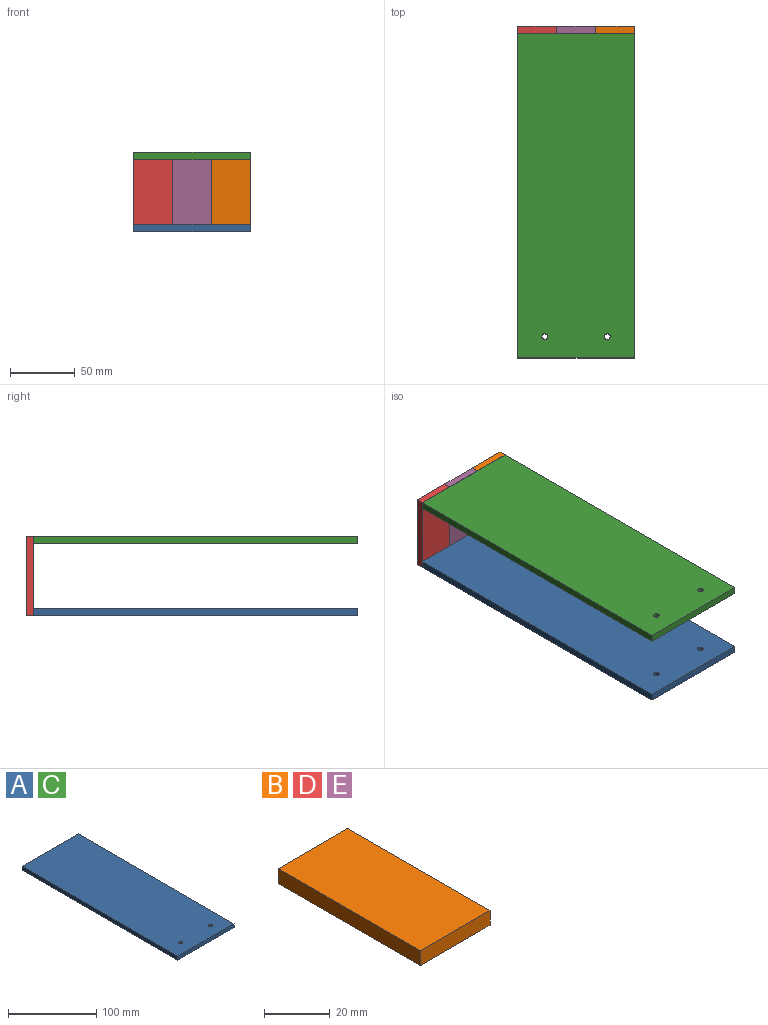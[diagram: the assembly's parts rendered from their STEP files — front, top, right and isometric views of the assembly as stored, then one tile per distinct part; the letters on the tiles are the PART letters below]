
ASSEMBLY  parts=5 mates=4
PART A: 10 faces, bbox 90x250x5.5 mm
  f0: plane 90x5.5mm, normal (0,1,0), area 495mm2, adj f1,f5,f6,f7
  f1: plane 250x5.5mm, normal (-1,0,0), area 1375mm2, adj f0,f2,f6,f7
  f2: plane 90x5.5mm, normal (0,-1,0), area 495mm2, adj f1,f5,f6,f7
  f3: cylinder r=2.25mm len=4.5mm, axis (0,0,-1), area 35.3mm2, adj f6,f8
  f4: cylinder r=2.25mm len=4.5mm, axis (0,0,-1), area 35.3mm2, adj f6,f9
  f5: plane 250x5.5mm, normal (1,0,0), area 1375mm2, adj f0,f2,f6,f7
  f6: plane 250x90mm, normal (0,0,1), area 22468.2mm2, adj f0,f1,f2,f3,f4,f5
  f7: plane 250x90mm, normal (0,0,-1), area 22326.8mm2, adj f0,f1,f2,f5,f8,f9
  f8: cone r=5.25mm half-angle=45deg, axis (0,0,-1), area 100mm2, adj f3,f7
  f9: cone r=5.25mm half-angle=45deg, axis (0,0,-1), area 100mm2, adj f4,f7
PART B: 6 faces, bbox 30x61x5.5 mm
  f0: plane 30x5.5mm, normal (0,1,0), area 165mm2, adj f1,f3,f4,f5
  f1: plane 61x5.5mm, normal (-1,0,0), area 335.5mm2, adj f0,f2,f4,f5
  f2: plane 30x5.5mm, normal (0,-1,0), area 165mm2, adj f1,f3,f4,f5
  f3: plane 61x5.5mm, normal (1,0,0), area 335.5mm2, adj f0,f2,f4,f5
  f4: plane 61x30mm, normal (0,0,1), area 1830mm2, adj f0,f1,f2,f3
  f5: plane 61x30mm, normal (0,0,-1), area 1830mm2, adj f0,f1,f2,f3
PART C: same geometry as A
PART D: same geometry as B
PART E: same geometry as B
PLACE A t=(-40.4,-87.75,38.5)mm
PLACE B rot(axis=(1,0,0),90deg) t=(-43.28,156.63,79.6)mm
PLACE C t=(-40.4,-87.75,94)mm
PLACE D rot(axis=(1,0,0),90deg) t=(-103.28,156.63,79.6)mm
PLACE E rot(axis=(1,0,0),90deg) t=(-73.28,156.63,79.6)mm
MATE fastened E.f4 <-> C.f0  axis (0,-1,0) through (-66.45,151.13,99.5)mm
MATE fastened B.f4 <-> C.f0  axis (0,-1,0) through (-21.45,151.13,99.5)mm
MATE fastened D.f4 <-> C.f0  axis (0,-1,0) through (-111.45,151.13,99.5)mm
MATE fastened A.f0 <-> D.f4  axis (0,-1,0) through (-111.45,151.13,38.5)mm
